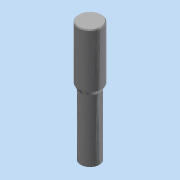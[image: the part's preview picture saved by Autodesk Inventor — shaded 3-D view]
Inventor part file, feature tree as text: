
AUTODESK INVENTOR PART (.ipt)
format: ipt  version: 2017 (Build 210142000, 142)  size: 243,712 bytes
history: native  units: mm
features: other x2, sketch x2, extrude x1
ambient origin geometry x8: Origin, YZ Plane, XZ Plane, XY Plane, X Axis, Y Axis, Z Axis, Center Point
bodies: Body1 (feature_tree)
feature tree (5):
  other  "Révolution1"
  extrude  "Extrusion4"  Depth=2.0mm
  sketch  "Esquisse4"
  sketch  "Esquisse5"
  other  "Projeter les arêtes coupées1"
